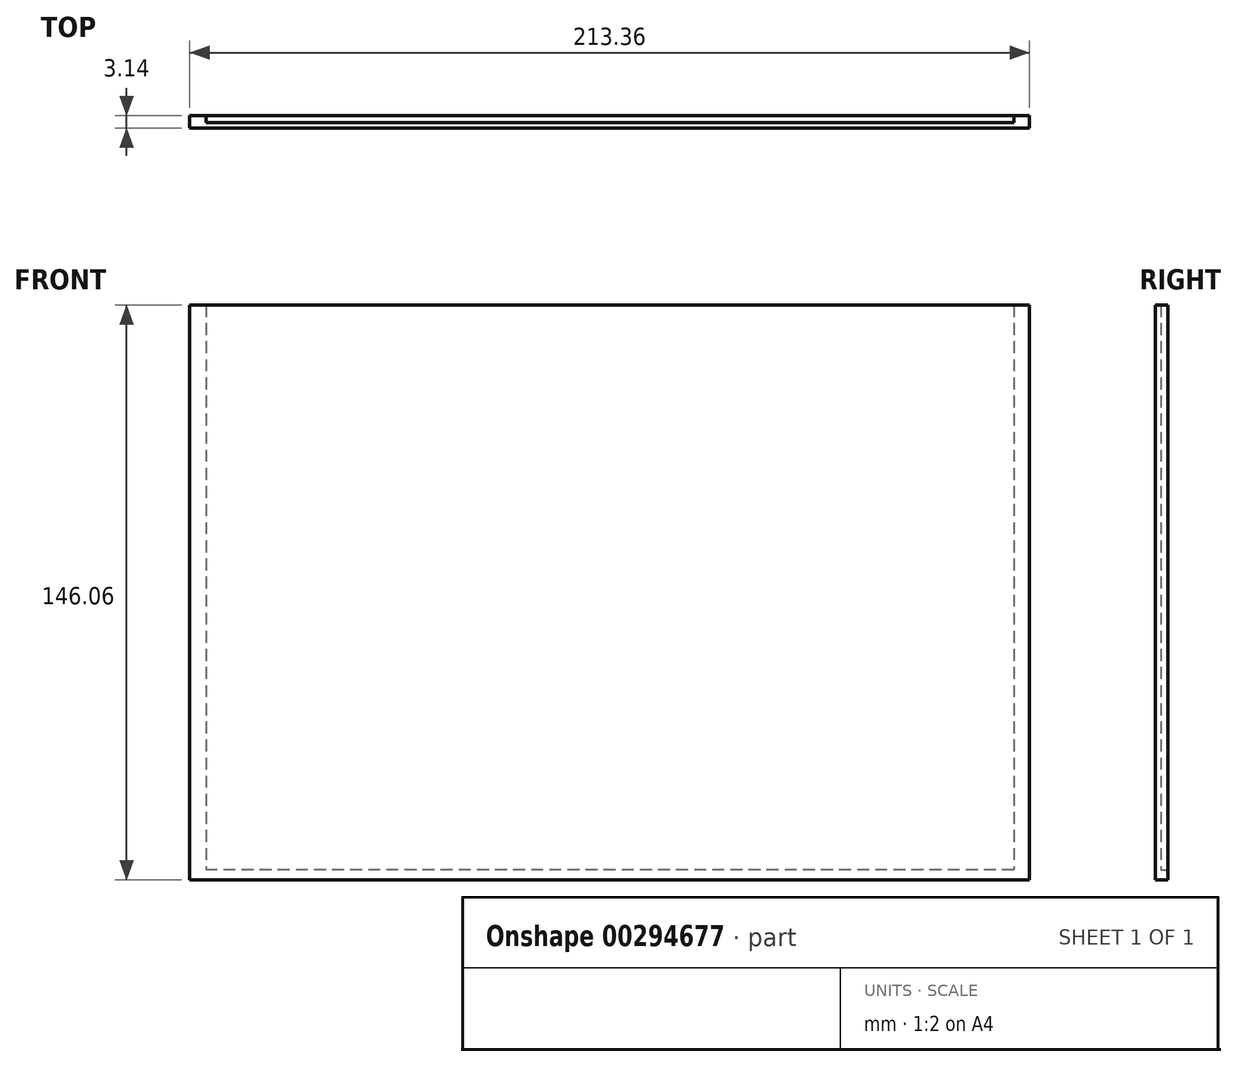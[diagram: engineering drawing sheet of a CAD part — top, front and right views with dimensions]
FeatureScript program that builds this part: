
annotation { "Feature Type Name" : "Feature", "Feature Type Description" : "" }
export const myFeature = defineFeature(function(context is Context, id is Id, definition is map)
    precondition{}
    {
        {
            var Q0;
            Q0=qCreatedBy(makeId("Front.planeOp"),FACE);
            var sketch = newSketch(context, id + "F0", { "sketchPlane" : qUnion([Q0])});
            skLineSegment(sketch, "E0.bottom", {"start": v(106.68, 73.03) * mm, "end": v(-106.68, 73.03) * mm});
            skLineSegment(sketch, "E0.top", {"start": v(106.68, -73.03) * mm, "end": v(-106.68, -73.03) * mm});
            skLineSegment(sketch, "E0.left", {"start": v(106.68, 73.03) * mm, "end": v(106.68, -73.03) * mm});
            skLineSegment(sketch, "E0.right", {"start": v(-106.68, 73.03) * mm, "end": v(-106.68, -73.03) * mm});
            skPoint(sketch, "E0.middle", {"position": v(0, 0) * mm});
            skSolve(sketch);
        }
        {
            var Q0;
            Q0 = qSketchRegion(id + "F0", true);
            extrude(context, id + "F1", {"entities" : qUnion([Q0]), "endBound" : BoundingType.SYMMETRIC, "depth" : 3.15 * mm});
        }
        {
            var Q0;
            Q0=makeQuery(id+"F1.opExtrude","CAP_FACE",FACE,{"disambiguationData":[OSD([sQuery(id+"F0.wireOp",EDGE,"E0.bottom"),sQuery(id+"F0.wireOp",EDGE,"E0.top"),sQuery(id+"F0.wireOp",EDGE,"E0.left"),sQuery(id+"F0.wireOp",EDGE,"E0.right")])],"isStart":true});
            var sketch = newSketch(context, id + "F2", { "sketchPlane" : qUnion([Q0])});
            skLineSegment(sketch, "E1.bottom", {"start": v(-102.73, 73.03) * mm, "end": v(102.56, 73.03) * mm});
            skLineSegment(sketch, "E1.top", {"start": v(-102.73, -70.48) * mm, "end": v(102.56, -70.48) * mm});
            skLineSegment(sketch, "E1.left", {"start": v(-102.73, 73.03) * mm, "end": v(-102.73, -70.48) * mm});
            skLineSegment(sketch, "E1.right", {"start": v(102.56, 73.03) * mm, "end": v(102.56, -70.48) * mm});
            skSolve(sketch);
        }
        {
            var Q0;
            Q0 = qSketchRegion(id + "F2", true);
            extrude(context, id + "F3", {"entities" : qUnion([Q0]), "operationType" : NewBodyOperationType.REMOVE, "oppositeDirection" : true, "depth" : 1.78 * mm});
        }
    });
